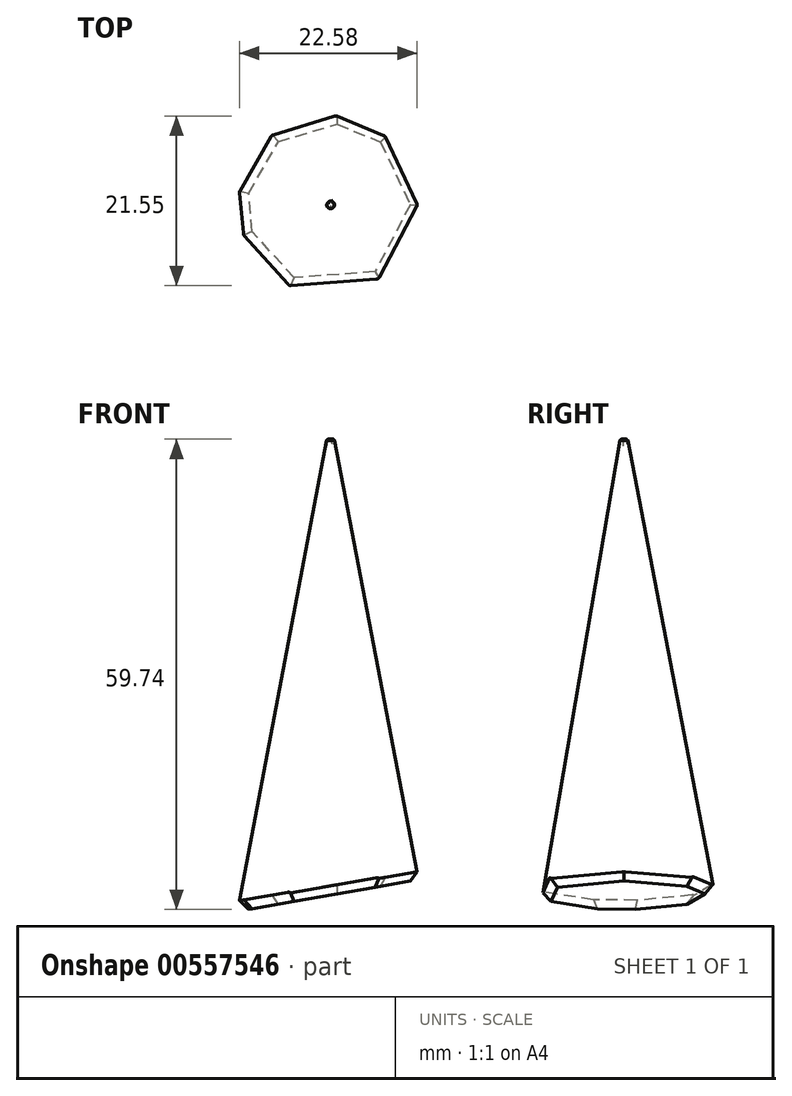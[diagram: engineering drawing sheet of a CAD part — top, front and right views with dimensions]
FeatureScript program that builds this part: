
annotation { "Feature Type Name" : "Feature", "Feature Type Description" : "" }
export const myFeature = defineFeature(function(context is Context, id is Id, definition is map)
    precondition{}
    {
        {
            var Q0;
            Q0=qCreatedBy(makeId("Top.planeOp"),FACE);
            cPlane(context, id + "F0", {"entities" : qUnion([Q0]), "cplaneType" : CPlaneType.OFFSET, "offset" : 60 * mm, "width" : 150 * mm, "height" : 150 * mm});
        }
        {
            var Q0;
            Q0=qCreatedBy(makeId("Top.planeOp"),FACE);
            var sketch = newSketch(context, id + "F1", { "sketchPlane" : qUnion([Q0])});
            skCircle(sketch, "E0", {"center": v(0, 0) * mm, "radius": 12 * mm, "construction": true});
            skLineSegment(sketch, "E1", {"start": v(-11.88, 1.7) * mm, "end": v(-7.77, 9.15) * mm});
            skLineSegment(sketch, "E2", {"start": v(-7.77, 9.15) * mm, "end": v(0.67, 11.98) * mm});
            skLineSegment(sketch, "E3", {"start": v(0.67, 11.98) * mm, "end": v(7.4, 9.44) * mm});
            skLineSegment(sketch, "E4", {"start": v(7.4, 9.44) * mm, "end": v(12, 0) * mm});
            skLineSegment(sketch, "E5", {"start": v(12, 0) * mm, "end": v(6.49, -10.1) * mm});
            skLineSegment(sketch, "E6", {"start": v(6.49, -10.1) * mm, "end": v(-5.5, -10.67) * mm});
            skLineSegment(sketch, "E7", {"start": v(-5.5, -10.67) * mm, "end": v(-11.37, -3.85) * mm});
            skLineSegment(sketch, "E8", {"start": v(-11.37, -3.85) * mm, "end": v(-11.88, 1.7) * mm});
            skSolve(sketch);
        }
        {
            var Q0;
            Q0=qCreatedBy(id+"F0.planeOp",FACE);
            var sketch = newSketch(context, id + "F2", { "sketchPlane" : qUnion([Q0])});
            skCircle(sketch, "E9", {"center": v(0, 0) * mm, "radius": 0.5 * mm, "construction": true});
            skPoint(sketch, "E10.0", {"position": v(-7.77, 9.15) * mm});
            skPoint(sketch, "E11.0", {"position": v(0.67, 11.98) * mm});
            skPoint(sketch, "E12.0", {"position": v(7.4, 9.44) * mm});
            skPoint(sketch, "E13.0", {"position": v(12, 0) * mm});
            skPoint(sketch, "E14.0", {"position": v(6.49, -10.1) * mm});
            skPoint(sketch, "E15.0", {"position": v(-5.5, -10.67) * mm});
            skPoint(sketch, "E16.0", {"position": v(-11.37, -3.85) * mm});
            skPoint(sketch, "E17.0", {"position": v(-11.88, 1.7) * mm});
            skLineSegment(sketch, "E18", {"start": v(0, 0) * mm, "end": v(-7.77, 9.15) * mm, "construction": true});
            skLineSegment(sketch, "E19", {"start": v(0, 0) * mm, "end": v(0.67, 11.98) * mm, "construction": true});
            skLineSegment(sketch, "E20", {"start": v(0, 0) * mm, "end": v(7.4, 9.44) * mm, "construction": true});
            skLineSegment(sketch, "E21", {"start": v(0, 0) * mm, "end": v(12, 0) * mm, "construction": true});
            skLineSegment(sketch, "E22", {"start": v(6.49, -10.1) * mm, "end": v(0, 0) * mm, "construction": true});
            skLineSegment(sketch, "E23", {"start": v(-5.5, -10.67) * mm, "end": v(0, 0) * mm, "construction": true});
            skLineSegment(sketch, "E24", {"start": v(-11.37, -3.85) * mm, "end": v(0, 0) * mm, "construction": true});
            skLineSegment(sketch, "E25", {"start": v(-11.88, 1.7) * mm, "end": v(0, 0) * mm, "construction": true});
            skLineSegment(sketch, "E26", {"start": v(0.03, 0.5) * mm, "end": v(0.3, 0.4) * mm});
            skLineSegment(sketch, "E27", {"start": v(0.3, 0.4) * mm, "end": v(0.5, 0) * mm});
            skLineSegment(sketch, "E28", {"start": v(0.5, 0) * mm, "end": v(0.27, -0.42) * mm});
            skLineSegment(sketch, "E29", {"start": v(0.27, -0.42) * mm, "end": v(-0.23, -0.44) * mm});
            skLineSegment(sketch, "E30", {"start": v(-0.23, -0.44) * mm, "end": v(-0.47, -0.16) * mm});
            skLineSegment(sketch, "E31", {"start": v(-0.47, -0.16) * mm, "end": v(-0.5, 0.07) * mm});
            skLineSegment(sketch, "E32", {"start": v(-0.5, 0.07) * mm, "end": v(-0.32, 0.38) * mm});
            skLineSegment(sketch, "E33", {"start": v(-0.32, 0.38) * mm, "end": v(0.03, 0.5) * mm});
            skSolve(sketch);
        }
        {
            var Q0;
            Q0 = qSketchRegion(id + "F2", true);
            var Q1;
            Q1 = qSketchRegion(id + "F1", true);
            loft(context, id + "F3", {"sheetProfilesArray" : [{ "sheetProfileEntities" : qUnion([Q0]) }, { "sheetProfileEntities" : qUnion([Q1]) }]});
        }
        {
            var Q0;
            Q0=qCreatedBy(makeId("Front.planeOp"),FACE);
            var sketch = newSketch(context, id + "F4", { "sketchPlane" : qUnion([Q0])});
            skLineSegment(sketch, "E34", {"start": v(-11.88, 0) * mm, "end": v(12, 4.21) * mm});
            skLineSegment(sketch, "E35", {"start": v(12, 4.21) * mm, "end": v(12, 0) * mm});
            skLineSegment(sketch, "E36", {"start": v(12, 0) * mm, "end": v(-11.88, 0) * mm});
            skSolve(sketch);
        }
        {
            var Q0;
            Q0 = qSketchRegion(id + "F4", true);
            extrude(context, id + "F5", {"entities" : qUnion([Q0]), "operationType" : NewBodyOperationType.REMOVE, "endBound" : BoundingType.THROUGH_ALL, "oppositeDirection" : true, "depth" : 25 * mm, "offsetDistance" : 25 * mm, "hasSecondDirection" : true, "secondDirectionBound" : BoundingType.THROUGH_ALL, "secondDirectionOppositeDirection" : false, "secondDirectionDepth" : 25 * mm});
        }
        {
            var Q0;
            Q0=makeQuery(id+"F5.boolean.opBoolean","INTERSECT",EDGE,{"derivedFrom":[makeQuery(id+"F3.opLoft","SWEPT_FACE",FACE,{"disambiguationData":[OSD([sQuery(id+"F1.wireOp",EDGE,"E5"),sQuery(id+"F1.wireOp",EDGE,"E6"),sQuery(id+"F1.wireOp",EDGE,"E7"),sQuery(id+"F2.wireOp",EDGE,"E28"),sQuery(id+"F2.wireOp",EDGE,"E29"),sQuery(id+"F2.wireOp",EDGE,"E30")])]}),makeQuery(id+"F5.opExtrude","SWEPT_FACE",FACE,{"disambiguationData":[OSD([sQuery(id+"F4.wireOp",EDGE,"E34")])]})]});
            var Q1;
            Q1=makeQuery(id+"F5.boolean.opBoolean","INTERSECT",EDGE,{"derivedFrom":[makeQuery(id+"F3.opLoft","SWEPT_FACE",FACE,{"disambiguationData":[OSD([sQuery(id+"F1.wireOp",EDGE,"E4"),sQuery(id+"F1.wireOp",EDGE,"E5"),sQuery(id+"F1.wireOp",EDGE,"E6"),sQuery(id+"F2.wireOp",EDGE,"E27"),sQuery(id+"F2.wireOp",EDGE,"E28"),sQuery(id+"F2.wireOp",EDGE,"E29")])]}),makeQuery(id+"F5.opExtrude","SWEPT_FACE",FACE,{"disambiguationData":[OSD([sQuery(id+"F4.wireOp",EDGE,"E34")])]})]});
            var Q2;
            Q2=makeQuery(id+"F5.boolean.opBoolean","INTERSECT",EDGE,{"derivedFrom":[makeQuery(id+"F3.opLoft","SWEPT_FACE",FACE,{"disambiguationData":[OSD([sQuery(id+"F1.wireOp",EDGE,"E6"),sQuery(id+"F1.wireOp",EDGE,"E7"),sQuery(id+"F1.wireOp",EDGE,"E8"),sQuery(id+"F2.wireOp",EDGE,"E29"),sQuery(id+"F2.wireOp",EDGE,"E30"),sQuery(id+"F2.wireOp",EDGE,"E31")])]}),makeQuery(id+"F5.opExtrude","SWEPT_FACE",FACE,{"disambiguationData":[OSD([sQuery(id+"F4.wireOp",EDGE,"E34")])]})]});
            var Q3;
            Q3=makeQuery(id+"F5.boolean.opBoolean","INTERSECT",EDGE,{"derivedFrom":[makeQuery(id+"F3.opLoft","SWEPT_FACE",FACE,{"disambiguationData":[OSD([sQuery(id+"F1.wireOp",EDGE,"E1"),sQuery(id+"F1.wireOp",EDGE,"E7"),sQuery(id+"F1.wireOp",EDGE,"E8"),sQuery(id+"F2.wireOp",EDGE,"E30"),sQuery(id+"F2.wireOp",EDGE,"E31"),sQuery(id+"F2.wireOp",EDGE,"E32")])]}),makeQuery(id+"F5.opExtrude","SWEPT_FACE",FACE,{"disambiguationData":[OSD([sQuery(id+"F4.wireOp",EDGE,"E34")])]})]});
            var Q4;
            Q4=makeQuery(id+"F5.boolean.opBoolean","INTERSECT",EDGE,{"derivedFrom":[makeQuery(id+"F3.opLoft","SWEPT_FACE",FACE,{"disambiguationData":[OSD([sQuery(id+"F1.wireOp",EDGE,"E3"),sQuery(id+"F1.wireOp",EDGE,"E4"),sQuery(id+"F1.wireOp",EDGE,"E5"),sQuery(id+"F2.wireOp",EDGE,"E26"),sQuery(id+"F2.wireOp",EDGE,"E27"),sQuery(id+"F2.wireOp",EDGE,"E28")])]}),makeQuery(id+"F5.opExtrude","SWEPT_FACE",FACE,{"disambiguationData":[OSD([sQuery(id+"F4.wireOp",EDGE,"E34")])]})]});
            var Q5;
            Q5=makeQuery(id+"F5.boolean.opBoolean","INTERSECT",EDGE,{"derivedFrom":[makeQuery(id+"F3.opLoft","SWEPT_FACE",FACE,{"disambiguationData":[OSD([sQuery(id+"F1.wireOp",EDGE,"E2"),sQuery(id+"F1.wireOp",EDGE,"E3"),sQuery(id+"F1.wireOp",EDGE,"E4"),sQuery(id+"F2.wireOp",EDGE,"E26"),sQuery(id+"F2.wireOp",EDGE,"E27"),sQuery(id+"F2.wireOp",EDGE,"E33")])]}),makeQuery(id+"F5.opExtrude","SWEPT_FACE",FACE,{"disambiguationData":[OSD([sQuery(id+"F4.wireOp",EDGE,"E34")])]})]});
            var Q6;
            Q6=makeQuery(id+"F5.boolean.opBoolean","INTERSECT",EDGE,{"derivedFrom":[makeQuery(id+"F3.opLoft","SWEPT_FACE",FACE,{"disambiguationData":[OSD([sQuery(id+"F1.wireOp",EDGE,"E1"),sQuery(id+"F1.wireOp",EDGE,"E2"),sQuery(id+"F1.wireOp",EDGE,"E3"),sQuery(id+"F2.wireOp",EDGE,"E26"),sQuery(id+"F2.wireOp",EDGE,"E32"),sQuery(id+"F2.wireOp",EDGE,"E33")])]}),makeQuery(id+"F5.opExtrude","SWEPT_FACE",FACE,{"disambiguationData":[OSD([sQuery(id+"F4.wireOp",EDGE,"E34")])]})]});
            var Q7;
            Q7=makeQuery(id+"F5.boolean.opBoolean","INTERSECT",EDGE,{"derivedFrom":[makeQuery(id+"F3.opLoft","SWEPT_FACE",FACE,{"disambiguationData":[OSD([sQuery(id+"F1.wireOp",EDGE,"E1"),sQuery(id+"F1.wireOp",EDGE,"E2"),sQuery(id+"F1.wireOp",EDGE,"E8"),sQuery(id+"F2.wireOp",EDGE,"E31"),sQuery(id+"F2.wireOp",EDGE,"E32"),sQuery(id+"F2.wireOp",EDGE,"E33")])]}),makeQuery(id+"F5.opExtrude","SWEPT_FACE",FACE,{"disambiguationData":[OSD([sQuery(id+"F4.wireOp",EDGE,"E34")])]})]});
            chamfer(context, id + "F6", {"entities" : qUnion([Q0, Q1, Q2, Q3, Q4, Q5, Q6, Q7]), "width" : 1 * mm, "tangentPropagation" : true});
        }
        {
            var Q0;
            Q0=makeQuery(id+"F3.opLoft","SWEPT_EDGE",EDGE,{"disambiguationData":[OSD([sQuery(id+"F1.wireOp",EDGE,"E5"),sQuery(id+"F1.wireOp",EDGE,"E6"),sQuery(id+"F2.wireOp",EDGE,"E28"),sQuery(id+"F2.wireOp",EDGE,"E29")])]});
            var Q1;
            Q1=makeQuery(id+"F3.opLoft","SWEPT_EDGE",EDGE,{"disambiguationData":[OSD([sQuery(id+"F1.wireOp",EDGE,"E6"),sQuery(id+"F1.wireOp",EDGE,"E7"),sQuery(id+"F2.wireOp",EDGE,"E29"),sQuery(id+"F2.wireOp",EDGE,"E30")])]});
            var Q2;
            Q2=makeQuery(id+"F3.opLoft","SWEPT_EDGE",EDGE,{"disambiguationData":[OSD([sQuery(id+"F1.wireOp",EDGE,"E4"),sQuery(id+"F1.wireOp",EDGE,"E5"),sQuery(id+"F2.wireOp",EDGE,"E27"),sQuery(id+"F2.wireOp",EDGE,"E28")])]});
            var Q3;
            Q3=makeQuery(id+"F3.opLoft","SWEPT_EDGE",EDGE,{"disambiguationData":[OSD([sQuery(id+"F1.wireOp",EDGE,"E3"),sQuery(id+"F1.wireOp",EDGE,"E4"),sQuery(id+"F2.wireOp",EDGE,"E26"),sQuery(id+"F2.wireOp",EDGE,"E27")])]});
            var Q4;
            Q4=makeQuery(id+"F3.opLoft","SWEPT_EDGE",EDGE,{"disambiguationData":[OSD([sQuery(id+"F1.wireOp",EDGE,"E2"),sQuery(id+"F1.wireOp",EDGE,"E3"),sQuery(id+"F2.wireOp",EDGE,"E26"),sQuery(id+"F2.wireOp",EDGE,"E33")])]});
            var Q5;
            Q5=makeQuery(id+"F3.opLoft","SWEPT_EDGE",EDGE,{"disambiguationData":[OSD([sQuery(id+"F1.wireOp",EDGE,"E7"),sQuery(id+"F1.wireOp",EDGE,"E8"),sQuery(id+"F2.wireOp",EDGE,"E30"),sQuery(id+"F2.wireOp",EDGE,"E31")])]});
            var Q6;
            Q6=makeQuery(id+"F3.opLoft","SWEPT_EDGE",EDGE,{"disambiguationData":[OSD([sQuery(id+"F1.wireOp",EDGE,"E1"),sQuery(id+"F1.wireOp",EDGE,"E8"),sQuery(id+"F2.wireOp",EDGE,"E31"),sQuery(id+"F2.wireOp",EDGE,"E32")])]});
            var Q7;
            Q7=makeQuery(id+"F3.opLoft","SWEPT_EDGE",EDGE,{"disambiguationData":[OSD([sQuery(id+"F1.wireOp",EDGE,"E1"),sQuery(id+"F1.wireOp",EDGE,"E2"),sQuery(id+"F2.wireOp",EDGE,"E32"),sQuery(id+"F2.wireOp",EDGE,"E33")])]});
            fillet(context, id + "F7", {"entities" : qUnion([Q0, Q1, Q2, Q3, Q4, Q5, Q6, Q7]), "radius" : 0.5 * mm, "tangentPropagation" : true, "allowEdgeOverflow" : false});
        }
        {
            var Q0;
            Q0=makeQuery(id+"F3.opLoft","CAP_FACE",FACE,{"disambiguationData":[OSD([makeQuery(id+"F2.imprint","IMPRINT",FACE,{"disambiguationData":[TD([[makeQuery(id+"F2.imprint","IMPRINT",EDGE,{"derivedFrom":sQuery(id+"F2.wireOp",EDGE,"E26")}),-1.0]])]})])],"isStart":true});
            fillet(context, id + "F8", {"entities" : qUnion([Q0]), "radius" : 0.2 * mm, "tangentPropagation" : true, "allowEdgeOverflow" : false});
        }
    });
